# Revit family: NBS_DuPontCorian_CntrTpWshBsns_BathSink_Rounded9310
name_source: partatom
category: Plumbing Fixtures
revit_build: Autodesk Revit 2014 (Build: 20130709_2115(x64)
units: mm (PartAtom-declared; Revit-internal decimal feet)

## types (1)
- 9310
    AccessibilityPerformance = http://www.dupont.co.uk
    AssetType = Fixed
    BIMObjectName = NBS_DuPontCorian_CounterTopWashBasins_BathSink_Rounded9310
    BasinDepth = 195 mm  [stored 0.639764 ft]
    BasinLength = 500 mm  [stored 1.64042 ft]
    BasinWidth = 500 mm  [stored 1.64042 ft]
    Category = Pr_40_20_96_18 : Counter top wash basins
    Color = Glacier White, Designer White
    CounterVoidLength = 450 mm  [stored 1.47638 ft]
    CounterVoidWidth = 450 mm  [stored 1.47638 ft]
    DeclarationOfPerformance = CL 25 - EN 14688:2006
    Default Elevation = 0 mm  [stored 0 ft]
    Description = A flexible Corian(R) solid surface composite material round kitchen sink or wash basin. Manufactured from natural minerals and acrylic resin. Designed to be seamlessly integrated into a Corian(R) surface.
    DrainSize = 46 mm
    DurationUnit = 40 years plus
    ExpectedLife = 40 years plus
    Features = Designed to be integrated into a Corian(R) surface. Available in the full colour range as standard or bespoke colours. Hygienic, easy to clean and maintain. Seamless joints.
    Finish = semi-gloss
    Form = Integrated or mounted under surface(undermount)
    IfcExportAs = IfcSanitaryTerminalType
    IfcExportType = WASHHANDBASIN
    IntegralAccessories = Includes overflow piece & 25mm diameteroverflow elbow; drain cover
    InternalDepth = 176
    InternalLength = 450
    InternalWidth = 450
    ManufacturerName = DuPont Corian
    ManufacturerURL = www.corian.co.uk
    Material = DuPont™ Corian® solid surface material
    ModelNumber = Rounded 9310
    ModelReference = Rounded 9310
    NBSCertification = http://www.nationalbimlibrary.com
    NBSDescription = Counter top wash basins
    NBSReference = 45-35-70/360
    Name = CounterTopWashBasins_BathSink_Rounded9310_DuPontCorian
    NominalDepth = 195 mm  [stored 0.639764 ft]
    NominalHeight = 195 mm  [stored 0.639764 ft]
    NominalLength = 495 mm
    NominalWidth = 500 mm  [stored 1.64042 ft]
    ProductInformation = www.dupont.co.uk/content/dam/dupont/products-and-services/construction-materials/surface-design-materials/documents/DuPont_Corian_Kitchen_and_Bathroom_Product_catalogue.pdf
    ReplacementCost = Repairable
    Shape = Circular
    SinkMaterial = NBS_Concept
    Size = d450 x 176
    SustainabilityPerformance = ISO 14001. Zero landfill at manufacturing site. Greenguard certified. Repairable nature makes lifetime performance 40 years plus.
    Uniclass2 = 45-31-79/418
    Uniclass2015Description = Counter top wash basins
    Uniclass2015Reference = Pr_40_20_96_18
    Uniclass2015Version = Products v1.1
    Version = 1
    WarrantyDescription = 10 year material warranty from DuPont(TM)
    WarrantyDurationParts = 10 years
    WarrantyDurationUnit = year
    WashHandBasinMounting = Integrated
    WashHandBasinType = Kitchen or HandRinse
    WasteOutletDiameter = 46 mm
    WaterSupplyOverflowAndWasteHolesOverflow = Round overflow hole with cover
    WaterSupplyOverflowAndWasteHolesWaste = No tapholes
    WaterSupplyOverflowAndWasteHolesWaterSupply = Round bottom waste outlet with drain cover

note: [stored X ft] marks values corroborated as IEEE doubles in the binary element streams (Revit-internal decimal feet)

## geometry (parser evidence)
native form markers: Sweep x5
no freeform markers — native parametric forms only
